# Revit family: Grille-Return-Carnes-RTAB-Steel_Grille
name_source: partatom
category: Duct Accessories
revit_build: Autodesk Revit MEP 2014 (Build: 20130308_1515(x64)
units: mm (PartAtom-declared; Revit-internal decimal feet)

## types (10) — shared parameters
Assembly Code = D3040100
Blade Spacing = 3/4"
Catalog = http://www.carnes.com
Default Elevation = 0"
Description = Square and Rectangular Registers and Grilles
Flow = 0 CFM
Manufacturer = CARNES COMPANY
Model = RTAB
Product Page URL = http://www.carnes.com
Return Connection = Diffuser Return Connector
Return Connector = Yes
Revit Object Download Link = http://library.smartbim.com
Specification Sheet = http://www.carnes.com
Subcatagory = Air Distribution
URL = http://www.carnes.com
Unit = Metal - Carnes - Steel Galvanized

## per-type parameters (varying)
| type | Duct Height | Duct Width | Height | Inner Depth | Inner Width | Width |
| RTAB 8 x 4 | 6" | 2" | 4" | 1 1/2" | 5 1/2" | 8" |
| RTAB 10 x 4 | 8" | 2" | 4" | 1 1/2" | 7 1/2" | 10" |
| RTAB 8 x 6 | 6" | 4" | 6" | 3 1/2" | 5 1/2" | 8" |
| RTAB 10 x 6 | 8" | 4" | 6" | 3 1/2" | 7 1/2" | 10" |
| RTAB 12 x 6 | 10" | 4" | 6" | 3 1/2" | 9 1/2" | 12" |
| RTAB 16 x 6 | 14" | 4" | 6" | 3 1/2" | 13 1/2" | 16" |
| RTAB 20 x 6 | 18" | 4" | 6" | 3 1/2" | 17 1/2" | 20" |
| RTAB 24 x 6 | 22" | 4" | 6" | 3 1/2" | 21 1/2" | 24" |
| RTAB 24 x 8 | 22" | 6" | 8" | 5 1/2" | 21 1/2" | 24" |
| RTAB 24 x 10 | 22" | 8" | 10" | 7 1/2" | 21 1/2" | 24" |

## geometry (parser evidence)
native form markers: Sweep x9
no freeform markers — native parametric forms only
